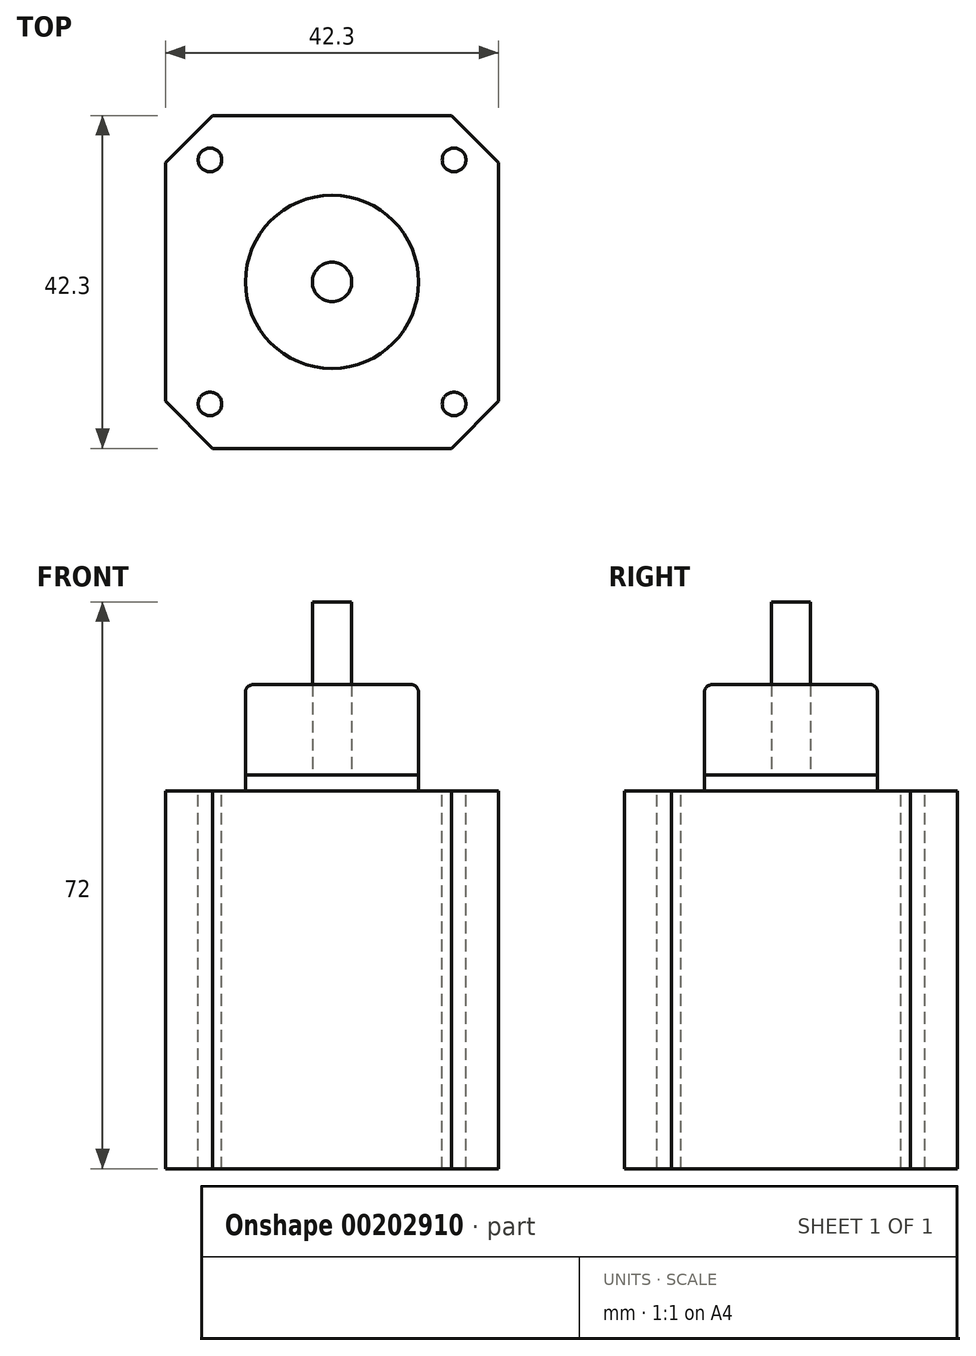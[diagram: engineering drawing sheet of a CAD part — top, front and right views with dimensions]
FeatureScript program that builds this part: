
annotation { "Feature Type Name" : "Feature", "Feature Type Description" : "" }
export const myFeature = defineFeature(function(context is Context, id is Id, definition is map)
    precondition{}
    {
        {
            var Q0;
            Q0=qCreatedBy(makeId("Top.planeOp"),FACE);
            var sketch = newSketch(context, id + "F0", { "sketchPlane" : qUnion([Q0])});
            skLineSegment(sketch, "E0.bottom", {"start": v(-21.15, 21.15) * mm, "end": v(21.15, 21.15) * mm});
            skLineSegment(sketch, "E0.top", {"start": v(-21.15, -21.15) * mm, "end": v(21.15, -21.15) * mm});
            skLineSegment(sketch, "E0.left", {"start": v(-21.15, 21.15) * mm, "end": v(-21.15, -21.15) * mm});
            skLineSegment(sketch, "E0.right", {"start": v(21.15, 21.15) * mm, "end": v(21.15, -21.15) * mm});
            skPoint(sketch, "E0.middle", {"position": v(0, 0) * mm});
            skSolve(sketch);
        }
        {
            var Q0;
            Q0=makeQuery(id+"F0.imprint","IMPRINT",FACE,{"disambiguationData":[TD([[makeQuery(id+"F0.imprint","IMPRINT",EDGE,{"derivedFrom":sQuery(id+"F0.wireOp",EDGE,"E0.bottom")}),-1.0]])]});
            extrude(context, id + "F1", {"entities" : qUnion([Q0]), "depth" : 48 * mm});
        }
        {
            var Q0;
            Q0=makeQuery(id+"F1.opExtrude","CAP_FACE",FACE,{"disambiguationData":[OSD([sQuery(id+"F0.wireOp",EDGE,"E0.bottom"),sQuery(id+"F0.wireOp",EDGE,"E0.top"),sQuery(id+"F0.wireOp",EDGE,"E0.left"),sQuery(id+"F0.wireOp",EDGE,"E0.right")])],"isStart":false});
            var sketch = newSketch(context, id + "F2", { "sketchPlane" : qUnion([Q0])});
            skCircle(sketch, "E1", {"center": v(0, 0) * mm, "radius": 11 * mm});
            skSolve(sketch);
        }
        {
            var Q0;
            Q0 = qSketchRegion(id + "F2", true);
            extrude(context, id + "F3", {"entities" : qUnion([Q0]), "operationType" : NewBodyOperationType.ADD, "depth" : 2 * mm});
        }
        {
            var Q0;
            Q0=makeQuery(id+"F3.opExtrude","CAP_FACE",FACE,{"disambiguationData":[OSD([sQuery(id+"F2.wireOp",EDGE,"E1")])],"isStart":false});
            var sketch = newSketch(context, id + "F4", { "sketchPlane" : qUnion([Q0])});
            skCircle(sketch, "E2", {"center": v(0, 0) * mm, "radius": 2.5 * mm});
            skSolve(sketch);
        }
        {
            var Q0;
            Q0 = qSketchRegion(id + "F4", true);
            extrude(context, id + "F5", {"entities" : qUnion([Q0]), "operationType" : NewBodyOperationType.ADD, "depth" : 22 * mm});
        }
        {
            var Q0;
            Q0=makeQuery(id+"F1.opExtrude","CAP_FACE",FACE,{"disambiguationData":[OSD([sQuery(id+"F0.wireOp",EDGE,"E0.bottom"),sQuery(id+"F0.wireOp",EDGE,"E0.top"),sQuery(id+"F0.wireOp",EDGE,"E0.left"),sQuery(id+"F0.wireOp",EDGE,"E0.right")])],"isStart":false});
            var sketch = newSketch(context, id + "F6", { "sketchPlane" : qUnion([Q0])});
            skPoint(sketch, "E3.middle", {"position": v(0, 0) * mm});
            skCircle(sketch, "E4", {"center": v(-15.5, 15.5) * mm, "radius": 1.5 * mm});
            skCircle(sketch, "E5", {"center": v(15.5, 15.5) * mm, "radius": 1.5 * mm});
            skCircle(sketch, "E6", {"center": v(-15.5, -15.5) * mm, "radius": 1.5 * mm});
            skCircle(sketch, "E7", {"center": v(15.5, -15.5) * mm, "radius": 1.5 * mm});
            skSolve(sketch);
        }
        {
            var Q0;
            Q0=makeQuery(id+"F6.imprint","IMPRINT",FACE,{"disambiguationData":[TD([[makeQuery(id+"F6.imprint","IMPRINT",EDGE,{"derivedFrom":sQuery(id+"F6.wireOp",EDGE,"E7")}),1.0]])]});
            var Q1;
            Q1=makeQuery(id+"F6.imprint","IMPRINT",FACE,{"disambiguationData":[TD([[makeQuery(id+"F6.imprint","IMPRINT",EDGE,{"derivedFrom":sQuery(id+"F6.wireOp",EDGE,"E5")}),1.0]])]});
            var Q2;
            Q2=makeQuery(id+"F6.imprint","IMPRINT",FACE,{"disambiguationData":[TD([[makeQuery(id+"F6.imprint","IMPRINT",EDGE,{"derivedFrom":sQuery(id+"F6.wireOp",EDGE,"E6")}),1.0]])]});
            var Q3;
            Q3=makeQuery(id+"F6.imprint","IMPRINT",FACE,{"disambiguationData":[TD([[makeQuery(id+"F6.imprint","IMPRINT",EDGE,{"derivedFrom":sQuery(id+"F6.wireOp",EDGE,"E4")}),1.0]])]});
            extrude(context, id + "F7", {"entities" : qUnion([Q0, Q1, Q2, Q3]), "operationType" : NewBodyOperationType.REMOVE, "oppositeDirection" : true, "depth" : 48 * mm});
        }
        {
            var Q0;
            Q0=makeQuery(id+"F1.opExtrude","SWEPT_EDGE",EDGE,{"disambiguationData":[OSD([sQuery(id+"F0.wireOp",EDGE,"E0.top"),sQuery(id+"F0.wireOp",EDGE,"E0.right")])]});
            var Q1;
            Q1=makeQuery(id+"F1.opExtrude","SWEPT_EDGE",EDGE,{"disambiguationData":[OSD([sQuery(id+"F0.wireOp",EDGE,"E0.top"),sQuery(id+"F0.wireOp",EDGE,"E0.left")])]});
            var Q2;
            Q2=makeQuery(id+"F1.opExtrude","SWEPT_EDGE",EDGE,{"disambiguationData":[OSD([sQuery(id+"F0.wireOp",EDGE,"E0.bottom"),sQuery(id+"F0.wireOp",EDGE,"E0.right")])]});
            var Q3;
            Q3=makeQuery(id+"F1.opExtrude","SWEPT_EDGE",EDGE,{"disambiguationData":[OSD([sQuery(id+"F0.wireOp",EDGE,"E0.bottom"),sQuery(id+"F0.wireOp",EDGE,"E0.left")])]});
            chamfer(context, id + "F8", {"entities" : qUnion([Q0, Q1, Q2, Q3]), "width" : 6 * mm, "tangentPropagation" : true});
        }
        {
            var Q0;
            Q0=makeQuery(id+"F3.opExtrude","CAP_FACE",FACE,{"disambiguationData":[OSD([sQuery(id+"F2.wireOp",EDGE,"E1")])],"isStart":false});
            var sketch = newSketch(context, id + "F9", { "sketchPlane" : qUnion([Q0])});
            skCircle(sketch, "E8", {"center": v(0, 0) * mm, "radius": 2.5 * mm});
            skCircle(sketch, "E9", {"center": v(0, 0) * mm, "radius": 11 * mm});
            skSolve(sketch);
        }
        {
            var Q0;
            Q0=makeQuery(id+"F9.imprint","IMPRINT",FACE,{"disambiguationData":[TD([[makeQuery(id+"F9.imprint","IMPRINT",EDGE,{"derivedFrom":sQuery(id+"F9.wireOp",EDGE,"E8")}),-1.0]])]});
            extrude(context, id + "F10", {"entities" : qUnion([Q0]), "depth" : 11.5 * mm});
        }
        {
            var Q0;
            Q0=makeQuery(id+"F10.opExtrude","CAP_EDGE",EDGE,{"disambiguationData":[OSD([sQuery(id+"F9.wireOp",EDGE,"E9")])],"isStart":false});
            fillet(context, id + "F11", {"entities" : qUnion([Q0]), "radius" : 1 * mm, "tangentPropagation" : true, "allowEdgeOverflow" : false});
        }
    });
